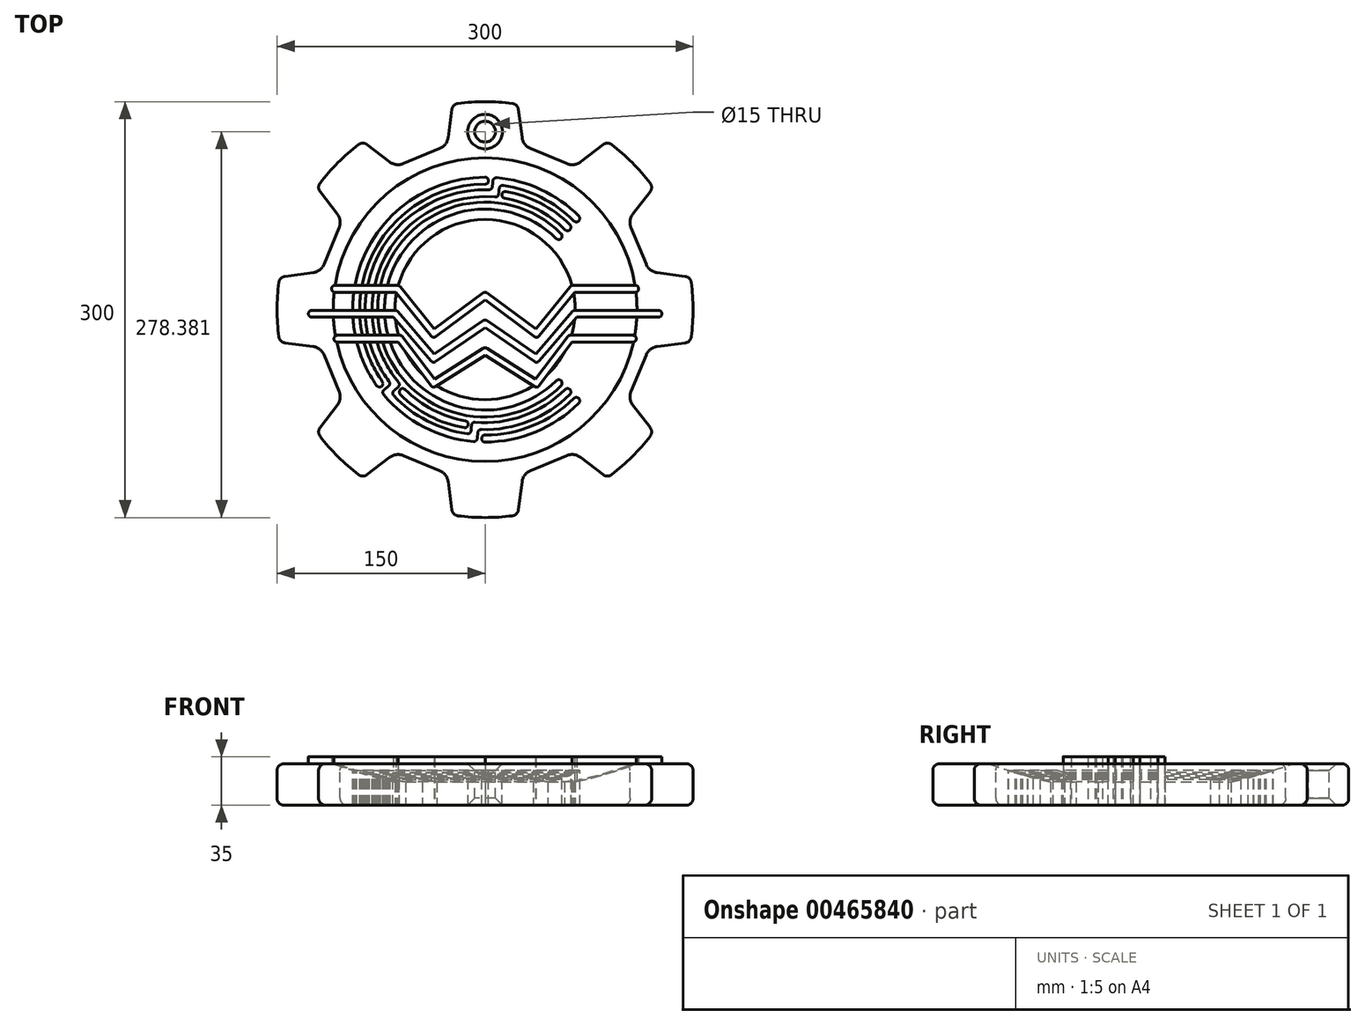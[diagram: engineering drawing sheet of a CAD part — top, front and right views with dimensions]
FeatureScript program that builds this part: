
annotation { "Feature Type Name" : "Feature", "Feature Type Description" : "" }
export const myFeature = defineFeature(function(context is Context, id is Id, definition is map)
    precondition{}
    {
        {
            var Q0;
            Q0=qCreatedBy(makeId("Top.planeOp"),FACE);
            var sketch = newSketch(context, id + "F0", { "sketchPlane" : qUnion([Q0])});
            skPoint(sketch, "E0.center", {"position": v(0, 0) * mm});
            skArc(sketch, "E1", {"start": v(53.03, 53.03) * mm, "mid": v(-75, 0) * mm, "end": v(53.03, -53.03) * mm, "construction": true});
            skLineSegment(sketch, "E2", {"start": v(0, 0) * mm, "end": v(74.3, 74.3) * mm, "construction": true});
            skLineSegment(sketch, "E3", {"start": v(0, 0) * mm, "end": v(73.03, -73.03) * mm, "construction": true});
            skArc(sketch, "E4.0.startCap", {"start": v(54.8, 54.8) * mm, "mid": v(54.8, 51.27) * mm, "end": v(51.27, 51.27) * mm});
            skArc(sketch, "E4.0.endCap", {"start": v(51.27, -51.27) * mm, "mid": v(54.8, -51.27) * mm, "end": v(54.8, -54.8) * mm});
            skArc(sketch, "E4.0.left", {"start": v(51.27, 51.27) * mm, "mid": v(-72.5, 0) * mm, "end": v(51.27, -51.27) * mm});
            skArc(sketch, "E4.0.right", {"start": v(54.8, 54.8) * mm, "mid": v(-77.5, 0) * mm, "end": v(54.8, -54.8) * mm});
            skLineSegment(sketch, "E5", {"start": v(0, 0) * mm, "end": v(18.29, 103.7) * mm, "construction": true});
            skPoint(sketch, "E6", {"position": v(14.59, 82.72) * mm});
            skPoint(sketch, "E7", {"position": v(59.4, 59.4) * mm});
            skArc(sketch, "E8", {"start": v(14.59, 82.72) * mm, "mid": v(10.96, 83.28) * mm, "end": v(7.32, 83.68) * mm, "construction": true});
            skArc(sketch, "E9", {"start": v(59.4, 59.4) * mm, "mid": v(38.79, 74.5) * mm, "end": v(14.59, 82.72) * mm, "construction": true});
            skLineSegment(sketch, "E10", {"start": v(0, 0) * mm, "end": v(9.32, 106.5) * mm, "construction": true});
            skPoint(sketch, "E11", {"position": v(65.76, 65.76) * mm});
            skPoint(sketch, "E12", {"position": v(8.1, 92.65) * mm});
            skPoint(sketch, "E13", {"position": v(7.32, 83.68) * mm});
            skArc(sketch, "E14", {"start": v(8.1, 92.65) * mm, "mid": v(4.06, 92.91) * mm, "end": v(0, 93) * mm, "construction": true});
            skArc(sketch, "E15", {"start": v(65.76, 65.76) * mm, "mid": v(39.3, 84.29) * mm, "end": v(8.1, 92.65) * mm, "construction": true});
            skArc(sketch, "E16.0.startCap", {"start": v(61.16, 61.16) * mm, "mid": v(61.16, 57.63) * mm, "end": v(57.63, 57.63) * mm});
            skArc(sketch, "E16.0.endCap", {"start": v(14.15, 80.26) * mm, "mid": v(12.12, 83.16) * mm, "end": v(15.02, 85.19) * mm});
            skArc(sketch, "E16.0.left", {"start": v(57.63, 57.63) * mm, "mid": v(37.63, 72.3) * mm, "end": v(14.15, 80.26) * mm});
            skArc(sketch, "E16.0.right", {"start": v(61.16, 61.16) * mm, "mid": v(39.94, 76.73) * mm, "end": v(15.02, 85.19) * mm});
            skLineSegment(sketch, "E17", {"start": v(0, 0) * mm, "end": v(-81.14, -68.08) * mm, "construction": true});
            skPoint(sketch, "E18", {"position": v(-64.35, -54) * mm});
            skPoint(sketch, "E19", {"position": v(-71.24, -59.78) * mm});
            skArc(sketch, "E20", {"start": v(-64.35, -54) * mm, "mid": v(-61.93, -56.75) * mm, "end": v(-59.4, -59.4) * mm, "construction": true});
            skArc(sketch, "E21", {"start": v(-71.24, -59.78) * mm, "mid": v(-42.94, -82.5) * mm, "end": v(-8.1, -92.65) * mm, "construction": true});
            skLineSegment(sketch, "E22", {"start": v(0, 0) * mm, "end": v(-9.7, -110.88) * mm, "construction": true});
            skPoint(sketch, "E23", {"position": v(-8.1, -92.65) * mm});
            skPoint(sketch, "E24", {"position": v(-7.32, -83.68) * mm});
            skArc(sketch, "E25", {"start": v(-7.32, -83.68) * mm, "mid": v(28.73, -78.93) * mm, "end": v(59.4, -59.4) * mm, "construction": true});
            skArc(sketch, "E26", {"start": v(-8.1, -92.65) * mm, "mid": v(-4.06, -92.91) * mm, "end": v(0, -93) * mm, "construction": true});
            skLineSegment(sketch, "E27", {"start": v(-64.35, -54) * mm, "end": v(-71.24, -59.78) * mm});
            skLineSegment(sketch, "E28", {"start": v(-7.32, -83.68) * mm, "end": v(-8.1, -92.65) * mm, "construction": true});
            skPoint(sketch, "E29", {"position": v(59.4, -59.4) * mm});
            skArc(sketch, "E30", {"start": v(59.4, -59.4) * mm, "mid": v(84, 0) * mm, "end": v(59.4, 59.4) * mm, "construction": true});
            skLineSegment(sketch, "E31", {"start": v(8.1, 92.65) * mm, "end": v(7.32, 83.68) * mm, "construction": true});
            skArc(sketch, "E32", {"start": v(7.32, 83.68) * mm, "mid": v(-74.5, 38.79) * mm, "end": v(-64.35, -54) * mm, "construction": true});
            skArc(sketch, "E33.0.startCap", {"start": v(5.61, 92.86) * mm, "mid": v(8.32, 95.14) * mm, "end": v(10.6, 92.43) * mm});
            skArc(sketch, "E33.0.endCap", {"start": v(9.81, 83.46) * mm, "mid": v(7.1, 81.19) * mm, "end": v(4.83, 83.9) * mm});
            skLineSegment(sketch, "E33.0.left", {"start": v(10.6, 92.43) * mm, "end": v(9.81, 83.46) * mm});
            skLineSegment(sketch, "E33.0.right", {"start": v(5.61, 92.86) * mm, "end": v(4.83, 83.9) * mm});
            skArc(sketch, "E34.0.startCap", {"start": v(-65.95, -52.08) * mm, "mid": v(-62.43, -52.39) * mm, "end": v(-62.74, -55.9) * mm});
            skArc(sketch, "E34.0.endCap", {"start": v(-69.64, -61.7) * mm, "mid": v(-73.16, -61.39) * mm, "end": v(-72.85, -57.86) * mm});
            skLineSegment(sketch, "E34.0.left", {"start": v(-62.74, -55.9) * mm, "end": v(-69.64, -61.7) * mm});
            skLineSegment(sketch, "E34.0.right", {"start": v(-65.95, -52.08) * mm, "end": v(-72.85, -57.86) * mm});
            skArc(sketch, "E34.1.startCap", {"start": v(-9.81, -83.46) * mm, "mid": v(-7.1, -81.19) * mm, "end": v(-4.83, -83.9) * mm});
            skArc(sketch, "E34.1.endCap", {"start": v(-5.61, -92.86) * mm, "mid": v(-8.32, -95.14) * mm, "end": v(-10.6, -92.43) * mm});
            skLineSegment(sketch, "E34.1.left", {"start": v(-4.83, -83.9) * mm, "end": v(-5.61, -92.86) * mm});
            skLineSegment(sketch, "E34.1.right", {"start": v(-9.81, -83.46) * mm, "end": v(-10.6, -92.43) * mm});
            skArc(sketch, "E35.0.startCap", {"start": v(-73.16, -61.39) * mm, "mid": v(-72.85, -57.86) * mm, "end": v(-69.33, -58.17) * mm});
            skArc(sketch, "E35.0.endCap", {"start": v(-7.89, -90.16) * mm, "mid": v(-5.61, -92.86) * mm, "end": v(-8.32, -95.14) * mm});
            skArc(sketch, "E35.0.left", {"start": v(-69.33, -58.17) * mm, "mid": v(-41.79, -80.27) * mm, "end": v(-7.89, -90.16) * mm});
            skArc(sketch, "E35.0.right", {"start": v(-73.16, -61.39) * mm, "mid": v(-44.1, -84.7) * mm, "end": v(-8.32, -95.14) * mm});
            skArc(sketch, "E35.1.startCap", {"start": v(-7.54, -86.17) * mm, "mid": v(-9.81, -83.46) * mm, "end": v(-7.1, -81.19) * mm});
            skArc(sketch, "E35.1.endCap", {"start": v(57.63, -57.63) * mm, "mid": v(61.16, -57.63) * mm, "end": v(61.16, -61.16) * mm});
            skArc(sketch, "E35.1.left", {"start": v(-7.1, -81.19) * mm, "mid": v(27.87, -76.58) * mm, "end": v(57.63, -57.63) * mm});
            skArc(sketch, "E35.1.right", {"start": v(-7.54, -86.17) * mm, "mid": v(29.58, -81.28) * mm, "end": v(61.16, -61.16) * mm});
            skArc(sketch, "E35.2.startCap", {"start": v(7.54, 86.17) * mm, "mid": v(9.81, 83.46) * mm, "end": v(7.1, 81.19) * mm});
            skArc(sketch, "E35.2.endCap", {"start": v(-62.43, -52.39) * mm, "mid": v(-62.74, -55.9) * mm, "end": v(-66.26, -55.6) * mm});
            skArc(sketch, "E35.2.left", {"start": v(7.1, 81.19) * mm, "mid": v(-72.3, 37.63) * mm, "end": v(-62.43, -52.39) * mm});
            skArc(sketch, "E35.2.right", {"start": v(7.54, 86.17) * mm, "mid": v(-76.73, 39.94) * mm, "end": v(-66.26, -55.6) * mm});
            skArc(sketch, "E35.3.startCap", {"start": v(67.53, 67.53) * mm, "mid": v(67.53, 64) * mm, "end": v(64, 64) * mm});
            skArc(sketch, "E35.3.endCap", {"start": v(7.89, 90.16) * mm, "mid": v(5.61, 92.86) * mm, "end": v(8.32, 95.14) * mm});
            skArc(sketch, "E35.3.left", {"start": v(64, 64) * mm, "mid": v(38.25, 82.02) * mm, "end": v(7.89, 90.16) * mm});
            skArc(sketch, "E35.3.right", {"start": v(67.53, 67.53) * mm, "mid": v(40.36, 86.55) * mm, "end": v(8.32, 95.14) * mm});
            skLineSegment(sketch, "E36", {"start": v(0, 0) * mm, "end": v(-93.02, -65.13) * mm, "construction": true});
            skPoint(sketch, "E37", {"position": v(-76.18, -53.34) * mm});
            skArc(sketch, "E38", {"start": v(-76.18, -53.34) * mm, "mid": v(-73.78, -56.61) * mm, "end": v(-71.24, -59.78) * mm, "construction": true});
            skLineSegment(sketch, "E39", {"start": v(0, 0) * mm, "end": v(0, -111.62) * mm, "construction": true});
            skPoint(sketch, "E40", {"position": v(0, -93) * mm});
            skArc(sketch, "E41", {"start": v(0, -93) * mm, "mid": v(35.59, -85.92) * mm, "end": v(65.76, -65.76) * mm, "construction": true});
            skPoint(sketch, "E42", {"position": v(65.76, -65.76) * mm});
            skArc(sketch, "E43", {"start": v(65.76, -65.76) * mm, "mid": v(93, 0) * mm, "end": v(65.76, 65.76) * mm, "construction": true});
            skLineSegment(sketch, "E44", {"start": v(0, 0) * mm, "end": v(0, 108.9) * mm, "construction": true});
            skPoint(sketch, "E45", {"position": v(0, 93) * mm});
            skArc(sketch, "E46", {"start": v(0, 93) * mm, "mid": v(-82.5, 42.94) * mm, "end": v(-76.18, -53.34) * mm, "construction": true});
            skArc(sketch, "E47.0.startCap", {"start": v(0, 95.5) * mm, "mid": v(2.5, 93) * mm, "end": v(0, 90.5) * mm});
            skArc(sketch, "E47.0.endCap", {"start": v(-74.13, -51.9) * mm, "mid": v(-74.75, -55.4) * mm, "end": v(-78.23, -54.78) * mm});
            skArc(sketch, "E47.0.left", {"start": v(0, 90.5) * mm, "mid": v(-80.27, 41.79) * mm, "end": v(-74.13, -51.9) * mm});
            skArc(sketch, "E47.0.right", {"start": v(0, 95.5) * mm, "mid": v(-84.7, 44.1) * mm, "end": v(-78.23, -54.78) * mm});
            skArc(sketch, "E47.1.startCap", {"start": v(0, -95.5) * mm, "mid": v(-2.5, -93) * mm, "end": v(0, -90.5) * mm});
            skArc(sketch, "E47.1.endCap", {"start": v(64, -64) * mm, "mid": v(67.53, -64) * mm, "end": v(67.53, -67.53) * mm});
            skArc(sketch, "E47.1.left", {"start": v(0, -90.5) * mm, "mid": v(34.63, -83.61) * mm, "end": v(64, -64) * mm});
            skArc(sketch, "E47.1.right", {"start": v(0, -95.5) * mm, "mid": v(36.55, -88.23) * mm, "end": v(67.53, -67.53) * mm});
            skLineSegment(sketch, "E48", {"start": v(0, 0) * mm, "end": v(-91.1, -91.1) * mm, "construction": true});
            skLineSegment(sketch, "E49", {"start": v(0, 0) * mm, "end": v(-19.76, -112.08) * mm, "construction": true});
            skPoint(sketch, "E50", {"position": v(-59.4, -59.4) * mm});
            skPoint(sketch, "E51", {"position": v(-14.59, -82.72) * mm});
            skArc(sketch, "E52", {"start": v(-59.4, -59.4) * mm, "mid": v(-38.79, -74.5) * mm, "end": v(-14.59, -82.72) * mm, "construction": true});
            skArc(sketch, "E53", {"start": v(-14.59, -82.72) * mm, "mid": v(-10.96, -83.28) * mm, "end": v(-7.32, -83.68) * mm, "construction": true});
            skArc(sketch, "E54.0.startCap", {"start": v(-61.16, -61.16) * mm, "mid": v(-61.16, -57.63) * mm, "end": v(-57.63, -57.63) * mm});
            skArc(sketch, "E54.0.endCap", {"start": v(-14.15, -80.26) * mm, "mid": v(-12.12, -83.16) * mm, "end": v(-15.02, -85.19) * mm});
            skArc(sketch, "E54.0.left", {"start": v(-57.63, -57.63) * mm, "mid": v(-37.63, -72.3) * mm, "end": v(-14.15, -80.26) * mm});
            skArc(sketch, "E54.0.right", {"start": v(-61.16, -61.16) * mm, "mid": v(-39.94, -76.73) * mm, "end": v(-15.02, -85.19) * mm});
            skSolve(sketch);
        }
        {
            var Q0;
            Q0=qCreatedBy(makeId("Top.planeOp"),FACE);
            var sketch = newSketch(context, id + "F1", { "sketchPlane" : qUnion([Q0])});
            skCircle(sketch, "E55", {"center": v(0, 0) * mm, "radius": 150 * mm});
            skLineSegment(sketch, "E56", {"start": v(-35, 145.86) * mm, "end": v(-20, 119.88) * mm});
            skLineSegment(sketch, "E57", {"start": v(-20, 119.88) * mm, "end": v(20, 119.88) * mm});
            skLineSegment(sketch, "E58", {"start": v(20, 119.88) * mm, "end": v(35, 145.86) * mm});
            skLineSegment(sketch, "E59.1.0", {"start": v(-127.89, 78.39) * mm, "end": v(-98.9, 70.62) * mm});
            skLineSegment(sketch, "E59.1.1", {"start": v(-98.9, 70.62) * mm, "end": v(-70.62, 98.9) * mm});
            skLineSegment(sketch, "E59.1.2", {"start": v(-70.62, 98.9) * mm, "end": v(-78.39, 127.89) * mm});
            skLineSegment(sketch, "E59.2.0", {"start": v(-145.86, -35) * mm, "end": v(-119.88, -20) * mm});
            skLineSegment(sketch, "E59.2.1", {"start": v(-119.88, -20) * mm, "end": v(-119.88, 20) * mm});
            skLineSegment(sketch, "E59.2.2", {"start": v(-119.88, 20) * mm, "end": v(-145.86, 35) * mm});
            skLineSegment(sketch, "E59.3.0", {"start": v(-78.39, -127.89) * mm, "end": v(-70.62, -98.9) * mm});
            skLineSegment(sketch, "E59.3.1", {"start": v(-70.62, -98.9) * mm, "end": v(-98.9, -70.62) * mm});
            skLineSegment(sketch, "E59.3.2", {"start": v(-98.9, -70.62) * mm, "end": v(-127.89, -78.39) * mm});
            skLineSegment(sketch, "E59.4.0", {"start": v(35, -145.86) * mm, "end": v(20, -119.88) * mm});
            skLineSegment(sketch, "E59.4.1", {"start": v(20, -119.88) * mm, "end": v(-20, -119.88) * mm});
            skLineSegment(sketch, "E59.4.2", {"start": v(-20, -119.88) * mm, "end": v(-35, -145.86) * mm});
            skLineSegment(sketch, "E59.5.0", {"start": v(127.89, -78.39) * mm, "end": v(98.9, -70.62) * mm});
            skLineSegment(sketch, "E59.5.1", {"start": v(98.9, -70.62) * mm, "end": v(70.62, -98.9) * mm});
            skLineSegment(sketch, "E59.5.2", {"start": v(70.62, -98.9) * mm, "end": v(78.39, -127.89) * mm});
            skLineSegment(sketch, "E59.6.0", {"start": v(145.86, 35) * mm, "end": v(119.88, 20) * mm});
            skLineSegment(sketch, "E59.6.1", {"start": v(119.88, 20) * mm, "end": v(119.88, -20) * mm});
            skLineSegment(sketch, "E59.6.2", {"start": v(119.88, -20) * mm, "end": v(145.86, -35) * mm});
            skLineSegment(sketch, "E59.7.0", {"start": v(78.39, 127.89) * mm, "end": v(70.62, 98.9) * mm});
            skLineSegment(sketch, "E59.7.1", {"start": v(70.62, 98.9) * mm, "end": v(98.9, 70.62) * mm});
            skLineSegment(sketch, "E59.7.2", {"start": v(98.9, 70.62) * mm, "end": v(127.89, 78.39) * mm});
            skCircle(sketch, "E60", {"center": v(0, 0) * mm, "radius": 65 * mm});
            skSolve(sketch);
        }
        {
            var Q0;
            Q0=qCreatedBy(makeId("Top.planeOp"),FACE);
            var sketch = newSketch(context, id + "F2", { "sketchPlane" : qUnion([Q0])});
            skLineSegment(sketch, "E61", {"start": v(-108.25, 15) * mm, "end": v(-63.25, 15) * mm, "construction": true});
            skLineSegment(sketch, "E62", {"start": v(-63.25, 15) * mm, "end": v(-37, -17.44) * mm, "construction": true});
            skLineSegment(sketch, "E63", {"start": v(-37, -17.44) * mm, "end": v(0, 10) * mm, "construction": true});
            skLineSegment(sketch, "E64", {"start": v(0, 10) * mm, "end": v(37, -17.44) * mm, "construction": true});
            skLineSegment(sketch, "E65", {"start": v(37, -17.44) * mm, "end": v(63.25, 15) * mm, "construction": true});
            skLineSegment(sketch, "E66", {"start": v(63.25, 15) * mm, "end": v(108.25, 15) * mm, "construction": true});
            skLineSegment(sketch, "E67", {"start": v(-124.93, -3) * mm, "end": v(-64.93, -3) * mm, "construction": true});
            skLineSegment(sketch, "E68", {"start": v(-64.93, -3) * mm, "end": v(-37, -35.44) * mm, "construction": true});
            skLineSegment(sketch, "E69", {"start": v(-37, -35.44) * mm, "end": v(0, -10) * mm, "construction": true});
            skLineSegment(sketch, "E70", {"start": v(0, -10) * mm, "end": v(37, -35.44) * mm, "construction": true});
            skLineSegment(sketch, "E71", {"start": v(37, -35.44) * mm, "end": v(64.93, -3) * mm, "construction": true});
            skLineSegment(sketch, "E72", {"start": v(64.93, -3) * mm, "end": v(124.93, -3) * mm, "construction": true});
            skLineSegment(sketch, "E73", {"start": v(-106.51, -21) * mm, "end": v(-61.51, -21) * mm, "construction": true});
            skLineSegment(sketch, "E74", {"start": v(-61.51, -21) * mm, "end": v(-37, -53.44) * mm, "construction": true});
            skLineSegment(sketch, "E75", {"start": v(-37, -53.44) * mm, "end": v(0, -30) * mm, "construction": true});
            skLineSegment(sketch, "E76", {"start": v(0, -30) * mm, "end": v(37, -53.44) * mm, "construction": true});
            skLineSegment(sketch, "E77", {"start": v(37, -53.44) * mm, "end": v(61.51, -21) * mm, "construction": true});
            skLineSegment(sketch, "E78", {"start": v(61.51, -21) * mm, "end": v(106.51, -21) * mm, "construction": true});
            skLineSegment(sketch, "E79", {"start": v(0, 45.3) * mm, "end": v(0, -49.42) * mm, "construction": true});
            skCircle(sketch, "E80", {"center": v(0, 0) * mm, "radius": 65 * mm, "construction": true});
            skLineSegment(sketch, "E81", {"start": v(-37, -53.44) * mm, "end": v(-37, 14.46) * mm, "construction": true});
            skArc(sketch, "E82.0.startCap", {"start": v(-106.51, -23.5) * mm, "mid": v(-109.01, -21) * mm, "end": v(-106.51, -18.5) * mm});
            skArc(sketch, "E82.0.endCap", {"start": v(-61.51, -18.5) * mm, "mid": v(-59.01, -21) * mm, "end": v(-61.51, -23.5) * mm});
            skLineSegment(sketch, "E82.0.left", {"start": v(-106.51, -18.5) * mm, "end": v(-61.51, -18.5) * mm});
            skLineSegment(sketch, "E82.0.right", {"start": v(-106.51, -23.5) * mm, "end": v(-61.51, -23.5) * mm});
            skArc(sketch, "E82.1.startCap", {"start": v(-124.93, -5.5) * mm, "mid": v(-127.43, -3) * mm, "end": v(-124.93, -0.5) * mm});
            skArc(sketch, "E82.1.endCap", {"start": v(-64.93, -0.5) * mm, "mid": v(-62.43, -3) * mm, "end": v(-64.93, -5.5) * mm});
            skLineSegment(sketch, "E82.1.left", {"start": v(-124.93, -0.5) * mm, "end": v(-64.93, -0.5) * mm});
            skLineSegment(sketch, "E82.1.right", {"start": v(-124.93, -5.5) * mm, "end": v(-64.93, -5.5) * mm});
            skArc(sketch, "E82.2.startCap", {"start": v(-108.25, 12.5) * mm, "mid": v(-110.75, 15) * mm, "end": v(-108.25, 17.5) * mm});
            skArc(sketch, "E82.2.endCap", {"start": v(-63.25, 17.5) * mm, "mid": v(-60.75, 15) * mm, "end": v(-63.25, 12.5) * mm});
            skLineSegment(sketch, "E82.2.left", {"start": v(-108.25, 17.5) * mm, "end": v(-63.25, 17.5) * mm});
            skLineSegment(sketch, "E82.2.right", {"start": v(-108.25, 12.5) * mm, "end": v(-63.25, 12.5) * mm});
            skArc(sketch, "E82.3.startCap", {"start": v(-65.19, 13.43) * mm, "mid": v(-64.82, 16.94) * mm, "end": v(-61.3, 16.57) * mm});
            skArc(sketch, "E82.3.endCap", {"start": v(-35.06, -15.87) * mm, "mid": v(-35.43, -19.39) * mm, "end": v(-38.94, -19.01) * mm});
            skLineSegment(sketch, "E82.3.left", {"start": v(-61.3, 16.57) * mm, "end": v(-35.06, -15.87) * mm});
            skLineSegment(sketch, "E82.3.right", {"start": v(-65.19, 13.43) * mm, "end": v(-38.94, -19.01) * mm});
            skArc(sketch, "E82.4.startCap", {"start": v(-66.83, -4.63) * mm, "mid": v(-66.56, -1.1) * mm, "end": v(-63.04, -1.37) * mm});
            skArc(sketch, "E82.4.endCap", {"start": v(-35.1, -33.81) * mm, "mid": v(-35.37, -37.34) * mm, "end": v(-38.9, -37.07) * mm});
            skLineSegment(sketch, "E82.4.left", {"start": v(-63.04, -1.37) * mm, "end": v(-35.1, -33.81) * mm});
            skLineSegment(sketch, "E82.4.right", {"start": v(-66.83, -4.63) * mm, "end": v(-38.9, -37.07) * mm});
            skArc(sketch, "E82.5.startCap", {"start": v(-63.5, -22.5) * mm, "mid": v(-63.02, -19) * mm, "end": v(-59.52, -19.5) * mm});
            skArc(sketch, "E82.5.endCap", {"start": v(-35, -51.93) * mm, "mid": v(-35.5, -55.44) * mm, "end": v(-39, -54.95) * mm});
            skLineSegment(sketch, "E82.5.left", {"start": v(-59.52, -19.5) * mm, "end": v(-35, -51.93) * mm});
            skLineSegment(sketch, "E82.5.right", {"start": v(-63.5, -22.5) * mm, "end": v(-39, -54.95) * mm});
            skArc(sketch, "E82.6.startCap", {"start": v(-35.51, -19.45) * mm, "mid": v(-39, -18.93) * mm, "end": v(-38.49, -15.43) * mm});
            skArc(sketch, "E82.6.endCap", {"start": v(-1.49, 12) * mm, "mid": v(2, 11.49) * mm, "end": v(1.49, 8) * mm});
            skLineSegment(sketch, "E82.6.left", {"start": v(-38.49, -15.43) * mm, "end": v(-1.49, 12) * mm});
            skLineSegment(sketch, "E82.6.right", {"start": v(-35.51, -19.45) * mm, "end": v(1.49, 8) * mm});
            skArc(sketch, "E82.7.startCap", {"start": v(-35.58, -37.5) * mm, "mid": v(-39.06, -36.86) * mm, "end": v(-38.42, -33.38) * mm});
            skArc(sketch, "E82.7.endCap", {"start": v(-1.42, -7.94) * mm, "mid": v(2.06, -8.58) * mm, "end": v(1.42, -12.06) * mm});
            skLineSegment(sketch, "E82.7.left", {"start": v(-38.42, -33.38) * mm, "end": v(-1.42, -7.94) * mm});
            skLineSegment(sketch, "E82.7.right", {"start": v(-35.58, -37.5) * mm, "end": v(1.42, -12.06) * mm});
            skArc(sketch, "E82.8.startCap", {"start": v(-35.66, -55.55) * mm, "mid": v(-39.11, -54.78) * mm, "end": v(-38.34, -51.33) * mm});
            skArc(sketch, "E82.8.endCap", {"start": v(-1.34, -27.89) * mm, "mid": v(2.11, -28.66) * mm, "end": v(1.34, -32.11) * mm});
            skLineSegment(sketch, "E82.8.left", {"start": v(-38.34, -51.33) * mm, "end": v(-1.34, -27.89) * mm});
            skLineSegment(sketch, "E82.8.right", {"start": v(-35.66, -55.55) * mm, "end": v(1.34, -32.11) * mm});
            skArc(sketch, "E82.9.startCap", {"start": v(-1.34, -32.11) * mm, "mid": v(-2.11, -28.66) * mm, "end": v(1.34, -27.89) * mm});
            skArc(sketch, "E82.9.endCap", {"start": v(38.34, -51.33) * mm, "mid": v(39.11, -54.78) * mm, "end": v(35.66, -55.55) * mm});
            skLineSegment(sketch, "E82.9.left", {"start": v(1.34, -27.89) * mm, "end": v(38.34, -51.33) * mm});
            skLineSegment(sketch, "E82.9.right", {"start": v(-1.34, -32.11) * mm, "end": v(35.66, -55.55) * mm});
            skArc(sketch, "E82.10.startCap", {"start": v(-1.42, -12.06) * mm, "mid": v(-2.06, -8.58) * mm, "end": v(1.42, -7.94) * mm});
            skArc(sketch, "E82.10.endCap", {"start": v(38.42, -33.38) * mm, "mid": v(39.06, -36.86) * mm, "end": v(35.58, -37.5) * mm});
            skLineSegment(sketch, "E82.10.left", {"start": v(1.42, -7.94) * mm, "end": v(38.42, -33.38) * mm});
            skLineSegment(sketch, "E82.10.right", {"start": v(-1.42, -12.06) * mm, "end": v(35.58, -37.5) * mm});
            skArc(sketch, "E82.11.startCap", {"start": v(-1.49, 8) * mm, "mid": v(-2, 11.49) * mm, "end": v(1.49, 12) * mm});
            skArc(sketch, "E82.11.endCap", {"start": v(38.49, -15.43) * mm, "mid": v(39, -18.93) * mm, "end": v(35.51, -19.45) * mm});
            skLineSegment(sketch, "E82.11.left", {"start": v(1.49, 12) * mm, "end": v(38.49, -15.43) * mm});
            skLineSegment(sketch, "E82.11.right", {"start": v(-1.49, 8) * mm, "end": v(35.51, -19.45) * mm});
            skArc(sketch, "E82.12.startCap", {"start": v(38.94, -19.01) * mm, "mid": v(35.43, -19.39) * mm, "end": v(35.06, -15.87) * mm});
            skArc(sketch, "E82.12.endCap", {"start": v(61.3, 16.57) * mm, "mid": v(64.82, 16.94) * mm, "end": v(65.19, 13.43) * mm});
            skLineSegment(sketch, "E82.12.left", {"start": v(35.06, -15.87) * mm, "end": v(61.3, 16.57) * mm});
            skLineSegment(sketch, "E82.12.right", {"start": v(38.94, -19.01) * mm, "end": v(65.19, 13.43) * mm});
            skArc(sketch, "E82.13.startCap", {"start": v(38.9, -37.07) * mm, "mid": v(35.37, -37.34) * mm, "end": v(35.1, -33.81) * mm});
            skArc(sketch, "E82.13.endCap", {"start": v(63.04, -1.37) * mm, "mid": v(66.56, -1.1) * mm, "end": v(66.83, -4.63) * mm});
            skLineSegment(sketch, "E82.13.left", {"start": v(35.1, -33.81) * mm, "end": v(63.04, -1.37) * mm});
            skLineSegment(sketch, "E82.13.right", {"start": v(38.9, -37.07) * mm, "end": v(66.83, -4.63) * mm});
            skArc(sketch, "E82.14.startCap", {"start": v(39, -54.95) * mm, "mid": v(35.5, -55.44) * mm, "end": v(35, -51.93) * mm});
            skArc(sketch, "E82.14.endCap", {"start": v(59.52, -19.5) * mm, "mid": v(63.02, -19) * mm, "end": v(63.5, -22.5) * mm});
            skLineSegment(sketch, "E82.14.left", {"start": v(35, -51.93) * mm, "end": v(59.52, -19.5) * mm});
            skLineSegment(sketch, "E82.14.right", {"start": v(39, -54.95) * mm, "end": v(63.5, -22.5) * mm});
            skArc(sketch, "E82.15.startCap", {"start": v(61.51, -23.5) * mm, "mid": v(59.01, -21) * mm, "end": v(61.51, -18.5) * mm});
            skArc(sketch, "E82.15.endCap", {"start": v(106.51, -18.5) * mm, "mid": v(109.01, -21) * mm, "end": v(106.51, -23.5) * mm});
            skLineSegment(sketch, "E82.15.left", {"start": v(61.51, -18.5) * mm, "end": v(106.51, -18.5) * mm});
            skLineSegment(sketch, "E82.15.right", {"start": v(61.51, -23.5) * mm, "end": v(106.51, -23.5) * mm});
            skArc(sketch, "E82.16.startCap", {"start": v(64.93, -5.5) * mm, "mid": v(62.43, -3) * mm, "end": v(64.93, -0.5) * mm});
            skArc(sketch, "E82.16.endCap", {"start": v(124.93, -0.5) * mm, "mid": v(127.43, -3) * mm, "end": v(124.93, -5.5) * mm});
            skLineSegment(sketch, "E82.16.left", {"start": v(64.93, -0.5) * mm, "end": v(124.93, -0.5) * mm});
            skLineSegment(sketch, "E82.16.right", {"start": v(64.93, -5.5) * mm, "end": v(124.93, -5.5) * mm});
            skArc(sketch, "E82.17.startCap", {"start": v(63.25, 12.5) * mm, "mid": v(60.75, 15) * mm, "end": v(63.25, 17.5) * mm});
            skArc(sketch, "E82.17.endCap", {"start": v(108.25, 17.5) * mm, "mid": v(110.75, 15) * mm, "end": v(108.25, 12.5) * mm});
            skLineSegment(sketch, "E82.17.left", {"start": v(63.25, 17.5) * mm, "end": v(108.25, 17.5) * mm});
            skLineSegment(sketch, "E82.17.right", {"start": v(63.25, 12.5) * mm, "end": v(108.25, 12.5) * mm});
            skSolve(sketch);
        }
        {
            var Q0;
            {var subQ8=sQuery(id+"F1.wireOp",EDGE,"E56");Q0=makeQuery(id+"F1.imprint","IMPRINT",FACE,{"disambiguationData":[TD([[makeQuery(id+"F1.imprint","IMPRINT",EDGE,{"derivedFrom":subQ8}),-1.0]])]});}
            extrude(context, id + "F3", {"entities" : qUnion([Q0]), "endBound" : BoundingType.SYMMETRIC, "depth" : 30 * mm});
        }
        {
            var Q0;
            Q0=makeQuery(id+"F3.opExtrude","SWEPT_BODY",BODY,{"disambiguationData":[OSD([sQuery(id+"F1.wireOp",EDGE,"E55"),sQuery(id+"F1.wireOp",EDGE,"E56"),sQuery(id+"F1.wireOp",EDGE,"E57"),sQuery(id+"F1.wireOp",EDGE,"E58"),sQuery(id+"F1.wireOp",EDGE,"E59.1.0"),sQuery(id+"F1.wireOp",EDGE,"E59.1.1"),sQuery(id+"F1.wireOp",EDGE,"E59.1.2"),sQuery(id+"F1.wireOp",EDGE,"E59.2.0"),sQuery(id+"F1.wireOp",EDGE,"E59.2.1"),sQuery(id+"F1.wireOp",EDGE,"E59.2.2"),sQuery(id+"F1.wireOp",EDGE,"E59.3.0"),sQuery(id+"F1.wireOp",EDGE,"E59.3.1"),sQuery(id+"F1.wireOp",EDGE,"E59.3.2"),sQuery(id+"F1.wireOp",EDGE,"E59.4.0"),sQuery(id+"F1.wireOp",EDGE,"E59.4.1"),sQuery(id+"F1.wireOp",EDGE,"E59.4.2"),sQuery(id+"F1.wireOp",EDGE,"E59.5.0"),sQuery(id+"F1.wireOp",EDGE,"E59.5.1"),sQuery(id+"F1.wireOp",EDGE,"E59.5.2"),sQuery(id+"F1.wireOp",EDGE,"E59.6.0"),sQuery(id+"F1.wireOp",EDGE,"E59.6.1"),sQuery(id+"F1.wireOp",EDGE,"E59.6.2"),sQuery(id+"F1.wireOp",EDGE,"E59.7.0"),sQuery(id+"F1.wireOp",EDGE,"E59.7.1"),sQuery(id+"F1.wireOp",EDGE,"E59.7.2"),sQuery(id+"F1.wireOp",EDGE,"E60")])]});
            var Q1;
            Q1=makeQuery(id+"F3.opExtrude","CAP_EDGE",EDGE,{"disambiguationData":[OSD([sQuery(id+"F1.wireOp",EDGE,"E60")])],"isStart":true});
            transform(context, id + "F4", {"entities" : qUnion([Q0]), "transformType" : TransformType.ROTATION, "transformAxis" : qUnion([Q1]), "angle" : 22.5 * degree, "makeCopy" : false});
        }
        {
            var Q0;
            Q0=qSketchRegion(id+"F0",true);
            extrude(context, id + "F5", {"entities" : qUnion([Q0]), "operationType" : NewBodyOperationType.REMOVE, "endBound" : BoundingType.SYMMETRIC, "oppositeDirection" : true, "depth" : 74 * mm});
        }
        {
            var Q0;
            Q0=makeQuery(id+"F5.boolean.opBoolean","COPY",EDGE,{"derivedFrom":makeQuery(id+"F5.opExtrude","SWEPT_EDGE",EDGE,{"disambiguationData":[OSD([sQuery(id+"F0.wireOp",EDGE,"E34.0.right"),sQuery(id+"F0.wireOp",EDGE,"E35.2.right")])]})});
            var Q1;
            Q1=makeQuery(id+"F5.boolean.opBoolean","COPY",EDGE,{"derivedFrom":makeQuery(id+"F5.opExtrude","SWEPT_EDGE",EDGE,{"disambiguationData":[OSD([sQuery(id+"F0.wireOp",EDGE,"E34.1.right"),sQuery(id+"F0.wireOp",EDGE,"E35.0.left")])]})});
            var Q2;
            Q2=makeQuery(id+"F5.boolean.opBoolean","COPY",EDGE,{"derivedFrom":makeQuery(id+"F5.opExtrude","SWEPT_EDGE",EDGE,{"disambiguationData":[OSD([sQuery(id+"F0.wireOp",EDGE,"E34.1.left"),sQuery(id+"F0.wireOp",EDGE,"E35.1.right")])]})});
            var Q3;
            Q3=makeQuery(id+"F5.boolean.opBoolean","COPY",EDGE,{"derivedFrom":makeQuery(id+"F5.opExtrude","SWEPT_EDGE",EDGE,{"disambiguationData":[OSD([sQuery(id+"F0.wireOp",EDGE,"E34.0.left"),sQuery(id+"F0.wireOp",EDGE,"E35.0.left")])]})});
            var Q4;
            Q4=makeQuery(id+"F5.boolean.opBoolean","COPY",EDGE,{"derivedFrom":makeQuery(id+"F5.opExtrude","SWEPT_EDGE",EDGE,{"disambiguationData":[OSD([sQuery(id+"F0.wireOp",EDGE,"E33.0.left"),sQuery(id+"F0.wireOp",EDGE,"E35.3.left")])]})});
            var Q5;
            Q5=makeQuery(id+"F5.boolean.opBoolean","COPY",EDGE,{"derivedFrom":makeQuery(id+"F5.opExtrude","SWEPT_EDGE",EDGE,{"disambiguationData":[OSD([sQuery(id+"F0.wireOp",EDGE,"E33.0.right"),sQuery(id+"F0.wireOp",EDGE,"E35.2.right")])]})});
            fillet(context, id + "F6", {"entities" : qUnion([Q0, Q1, Q2, Q3, Q4, Q5]), "radius" : 2.5 * mm, "tangentPropagation" : true, "allowEdgeOverflow" : false});
        }
        {
            var Q0;
            Q0=makeQuery(id+"F3.opExtrude","SWEPT_EDGE",EDGE,{"disambiguationData":[OSD([sQuery(id+"F1.wireOp",EDGE,"E59.1.0"),sQuery(id+"F1.wireOp",EDGE,"E59.1.1")])]});
            var Q1;
            Q1=makeQuery(id+"F3.opExtrude","SWEPT_EDGE",EDGE,{"disambiguationData":[OSD([sQuery(id+"F1.wireOp",EDGE,"E59.1.1"),sQuery(id+"F1.wireOp",EDGE,"E59.1.2")])]});
            var Q2;
            Q2=makeQuery(id+"F3.opExtrude","SWEPT_EDGE",EDGE,{"disambiguationData":[OSD([sQuery(id+"F1.wireOp",EDGE,"E56"),sQuery(id+"F1.wireOp",EDGE,"E57")])]});
            var Q3;
            Q3=makeQuery(id+"F3.opExtrude","SWEPT_EDGE",EDGE,{"disambiguationData":[OSD([sQuery(id+"F1.wireOp",EDGE,"E57"),sQuery(id+"F1.wireOp",EDGE,"E58")])]});
            var Q4;
            Q4=makeQuery(id+"F3.opExtrude","SWEPT_EDGE",EDGE,{"disambiguationData":[OSD([sQuery(id+"F1.wireOp",EDGE,"E59.7.0"),sQuery(id+"F1.wireOp",EDGE,"E59.7.1")])]});
            var Q5;
            Q5=makeQuery(id+"F3.opExtrude","SWEPT_EDGE",EDGE,{"disambiguationData":[OSD([sQuery(id+"F1.wireOp",EDGE,"E59.7.1"),sQuery(id+"F1.wireOp",EDGE,"E59.7.2")])]});
            var Q6;
            Q6=makeQuery(id+"F3.opExtrude","SWEPT_EDGE",EDGE,{"disambiguationData":[OSD([sQuery(id+"F1.wireOp",EDGE,"E59.6.0"),sQuery(id+"F1.wireOp",EDGE,"E59.6.1")])]});
            var Q7;
            Q7=makeQuery(id+"F3.opExtrude","SWEPT_EDGE",EDGE,{"disambiguationData":[OSD([sQuery(id+"F1.wireOp",EDGE,"E59.6.1"),sQuery(id+"F1.wireOp",EDGE,"E59.6.2")])]});
            var Q8;
            Q8=makeQuery(id+"F3.opExtrude","SWEPT_EDGE",EDGE,{"disambiguationData":[OSD([sQuery(id+"F1.wireOp",EDGE,"E59.5.0"),sQuery(id+"F1.wireOp",EDGE,"E59.5.1")])]});
            var Q9;
            Q9=makeQuery(id+"F3.opExtrude","SWEPT_EDGE",EDGE,{"disambiguationData":[OSD([sQuery(id+"F1.wireOp",EDGE,"E59.5.1"),sQuery(id+"F1.wireOp",EDGE,"E59.5.2")])]});
            var Q10;
            Q10=makeQuery(id+"F3.opExtrude","SWEPT_EDGE",EDGE,{"disambiguationData":[OSD([sQuery(id+"F1.wireOp",EDGE,"E59.4.0"),sQuery(id+"F1.wireOp",EDGE,"E59.4.1")])]});
            var Q11;
            Q11=makeQuery(id+"F3.opExtrude","SWEPT_EDGE",EDGE,{"disambiguationData":[OSD([sQuery(id+"F1.wireOp",EDGE,"E59.4.1"),sQuery(id+"F1.wireOp",EDGE,"E59.4.2")])]});
            var Q12;
            Q12=makeQuery(id+"F3.opExtrude","SWEPT_EDGE",EDGE,{"disambiguationData":[OSD([sQuery(id+"F1.wireOp",EDGE,"E59.3.0"),sQuery(id+"F1.wireOp",EDGE,"E59.3.1")])]});
            var Q13;
            Q13=makeQuery(id+"F3.opExtrude","SWEPT_EDGE",EDGE,{"disambiguationData":[OSD([sQuery(id+"F1.wireOp",EDGE,"E59.3.1"),sQuery(id+"F1.wireOp",EDGE,"E59.3.2")])]});
            var Q14;
            Q14=makeQuery(id+"F3.opExtrude","SWEPT_EDGE",EDGE,{"disambiguationData":[OSD([sQuery(id+"F1.wireOp",EDGE,"E59.2.0"),sQuery(id+"F1.wireOp",EDGE,"E59.2.1")])]});
            var Q15;
            Q15=makeQuery(id+"F3.opExtrude","SWEPT_EDGE",EDGE,{"disambiguationData":[OSD([sQuery(id+"F1.wireOp",EDGE,"E59.2.1"),sQuery(id+"F1.wireOp",EDGE,"E59.2.2")])]});
            fillet(context, id + "F7", {"entities" : qUnion([Q0, Q1, Q2, Q3, Q4, Q5, Q6, Q7, Q8, Q9, Q10, Q11, Q12, Q13, Q14, Q15]), "radius" : 10 * mm, "tangentPropagation" : true, "allowEdgeOverflow" : false});
        }
        {
            var Q0;
            Q0=qCreatedBy(makeId("Front.planeOp"),FACE);
            var sketch = newSketch(context, id + "F8", { "sketchPlane" : qUnion([Q0])});
            skArc(sketch, "E83", {"start": v(-310, 305) * mm, "mid": v(0, -5) * mm, "end": v(310, 305) * mm});
            skLineSegment(sketch, "E84", {"start": v(0, 305) * mm, "end": v(0, 15) * mm});
            skLineSegment(sketch, "E85", {"start": v(-310, 305) * mm, "end": v(310, 305) * mm});
            skSolve(sketch);
        }
        {
            var Q0;
            Q0=qSketchRegion(id+"F8",true);
            var Q1;
            Q1=sQuery(id+"F8.wireOp",EDGE,"E85");
            revolve(context, id + "F9", {"entities" : qUnion([Q0]), "axis" : qUnion([Q1]), "revolveType" : RevolveType.SYMMETRIC, "angle" : 84.04 * degree});
        }
        {
            var Q0;
            Q0=makeQuery(id+"F9.opRevolve","SWEPT_BODY",BODY,{"disambiguationData":[OSD([sQuery(id+"F8.wireOp",EDGE,"E83"),sQuery(id+"F8.wireOp",EDGE,"E85")])]});
            var Q1;
            Q1=makeQuery(id+"F3.opExtrude","SWEPT_BODY",BODY,{"disambiguationData":[OSD([sQuery(id+"F1.wireOp",EDGE,"E55"),sQuery(id+"F1.wireOp",EDGE,"E56"),sQuery(id+"F1.wireOp",EDGE,"E57"),sQuery(id+"F1.wireOp",EDGE,"E58"),sQuery(id+"F1.wireOp",EDGE,"E59.1.0"),sQuery(id+"F1.wireOp",EDGE,"E59.1.1"),sQuery(id+"F1.wireOp",EDGE,"E59.1.2"),sQuery(id+"F1.wireOp",EDGE,"E59.2.0"),sQuery(id+"F1.wireOp",EDGE,"E59.2.1"),sQuery(id+"F1.wireOp",EDGE,"E59.2.2"),sQuery(id+"F1.wireOp",EDGE,"E59.3.0"),sQuery(id+"F1.wireOp",EDGE,"E59.3.1"),sQuery(id+"F1.wireOp",EDGE,"E59.3.2"),sQuery(id+"F1.wireOp",EDGE,"E59.4.0"),sQuery(id+"F1.wireOp",EDGE,"E59.4.1"),sQuery(id+"F1.wireOp",EDGE,"E59.4.2"),sQuery(id+"F1.wireOp",EDGE,"E59.5.0"),sQuery(id+"F1.wireOp",EDGE,"E59.5.1"),sQuery(id+"F1.wireOp",EDGE,"E59.5.2"),sQuery(id+"F1.wireOp",EDGE,"E59.6.0"),sQuery(id+"F1.wireOp",EDGE,"E59.6.1"),sQuery(id+"F1.wireOp",EDGE,"E59.6.2"),sQuery(id+"F1.wireOp",EDGE,"E59.7.0"),sQuery(id+"F1.wireOp",EDGE,"E59.7.1"),sQuery(id+"F1.wireOp",EDGE,"E59.7.2"),sQuery(id+"F1.wireOp",EDGE,"E60")])]});
            booleanBodies(context, id + "F10", {"operationType" : BooleanOperationType.SUBTRACTION, "tools" : qUnion([Q0]), "targets" : qUnion([Q1])});
        }
        {
            var Q0;
            Q0=qSketchRegion(id+"F2",true);
            extrude(context, id + "F11", {"entities" : qUnion([Q0]), "operationType" : NewBodyOperationType.ADD, "depth" : 20 * mm});
        }
        {
            var Q0;
            Q0=qSketchRegion(id+"F2",true);
            extrude(context, id + "F12", {"entities" : qUnion([Q0]), "operationType" : NewBodyOperationType.ADD, "oppositeDirection" : true, "depth" : 15 * mm});
        }
        {
            var Q0;
            Q0=makeQuery(id+"F3.opExtrude","SWEPT_FACE",FACE,{"disambiguationData":[OSD([sQuery(id+"F1.wireOp",EDGE,"E59.2.1")])]});
            var Q1;
            Q1=makeQuery(id+"F7.opFillet","BLEND_FACE",FACE,{"disambiguationData":[OSD([sQuery(id+"F1.wireOp",EDGE,"E59.2.1"),sQuery(id+"F1.wireOp",EDGE,"E59.2.2")])]});
            var Q2;
            Q2=makeQuery(id+"F3.opExtrude","SWEPT_FACE",FACE,{"disambiguationData":[OSD([sQuery(id+"F1.wireOp",EDGE,"E59.2.2")])]});
            var Q3;
            {var subQ0=sQuery(id+"F1.wireOp",EDGE,"E55");Q3=makeQuery(id+"F3.opExtrude","SWEPT_FACE",FACE,{"disambiguationData":[OSD([subQ0]),TDD([makeQuery(id+"F1.imprint","IMPRINT",EDGE,{"disambiguationData":[TD([[makeQuery(id+"F1.imprint","INTERSECT",VERTEX,{"derivedFrom":[subQ0,sQuery(id+"F1.wireOp",EDGE,"E59.1.0")]}),-1.0]])],"derivedFrom":subQ0})])]});}
            var Q4;
            Q4=makeQuery(id+"F7.opFillet","BLEND_FACE",FACE,{"disambiguationData":[OSD([sQuery(id+"F1.wireOp",EDGE,"E59.2.0"),sQuery(id+"F1.wireOp",EDGE,"E59.2.1")])]});
            var Q5;
            Q5=makeQuery(id+"F3.opExtrude","SWEPT_FACE",FACE,{"disambiguationData":[OSD([sQuery(id+"F1.wireOp",EDGE,"E59.2.0")])]});
            var Q6;
            {var subQ0=sQuery(id+"F1.wireOp",EDGE,"E55");Q6=makeQuery(id+"F3.opExtrude","SWEPT_FACE",FACE,{"disambiguationData":[OSD([subQ0]),TDD([makeQuery(id+"F1.imprint","IMPRINT",EDGE,{"disambiguationData":[TD([[makeQuery(id+"F1.imprint","INTERSECT",VERTEX,{"derivedFrom":[subQ0,sQuery(id+"F1.wireOp",EDGE,"E59.2.0")]}),-1.0]])],"derivedFrom":subQ0})])]});}
            var Q7;
            Q7=makeQuery(id+"F3.opExtrude","SWEPT_FACE",FACE,{"disambiguationData":[OSD([sQuery(id+"F1.wireOp",EDGE,"E59.3.2")])]});
            var Q8;
            Q8=makeQuery(id+"F7.opFillet","BLEND_FACE",FACE,{"disambiguationData":[OSD([sQuery(id+"F1.wireOp",EDGE,"E59.3.1"),sQuery(id+"F1.wireOp",EDGE,"E59.3.2")])]});
            var Q9;
            Q9=makeQuery(id+"F3.opExtrude","SWEPT_FACE",FACE,{"disambiguationData":[OSD([sQuery(id+"F1.wireOp",EDGE,"E59.3.1")])]});
            var Q10;
            Q10=makeQuery(id+"F7.opFillet","BLEND_FACE",FACE,{"disambiguationData":[OSD([sQuery(id+"F1.wireOp",EDGE,"E59.3.0"),sQuery(id+"F1.wireOp",EDGE,"E59.3.1")])]});
            var Q11;
            {var subQ0=sQuery(id+"F1.wireOp",EDGE,"E55");Q11=makeQuery(id+"F3.opExtrude","SWEPT_FACE",FACE,{"disambiguationData":[OSD([subQ0]),TDD([makeQuery(id+"F1.imprint","IMPRINT",EDGE,{"disambiguationData":[TD([[makeQuery(id+"F1.imprint","INTERSECT",VERTEX,{"derivedFrom":[subQ0,sQuery(id+"F1.wireOp",EDGE,"E59.3.0")]}),-1.0]])],"derivedFrom":subQ0})])]});}
            var Q12;
            Q12=makeQuery(id+"F3.opExtrude","SWEPT_FACE",FACE,{"disambiguationData":[OSD([sQuery(id+"F1.wireOp",EDGE,"E59.3.0")])]});
            var Q13;
            Q13=makeQuery(id+"F3.opExtrude","SWEPT_EDGE",EDGE,{"disambiguationData":[OSD([sQuery(id+"F1.wireOp",EDGE,"E55"),sQuery(id+"F1.wireOp",EDGE,"E59.3.0")])]});
            var Q14;
            Q14=makeQuery(id+"F3.opExtrude","SWEPT_FACE",FACE,{"disambiguationData":[OSD([sQuery(id+"F1.wireOp",EDGE,"E59.4.2")])]});
            var Q15;
            Q15=makeQuery(id+"F7.opFillet","BLEND_FACE",FACE,{"disambiguationData":[OSD([sQuery(id+"F1.wireOp",EDGE,"E59.4.1"),sQuery(id+"F1.wireOp",EDGE,"E59.4.2")])]});
            var Q16;
            Q16=makeQuery(id+"F3.opExtrude","SWEPT_FACE",FACE,{"disambiguationData":[OSD([sQuery(id+"F1.wireOp",EDGE,"E59.4.1")])]});
            var Q17;
            Q17=makeQuery(id+"F7.opFillet","BLEND_FACE",FACE,{"disambiguationData":[OSD([sQuery(id+"F1.wireOp",EDGE,"E59.4.0"),sQuery(id+"F1.wireOp",EDGE,"E59.4.1")])]});
            var Q18;
            Q18=makeQuery(id+"F3.opExtrude","SWEPT_FACE",FACE,{"disambiguationData":[OSD([sQuery(id+"F1.wireOp",EDGE,"E59.4.0")])]});
            var Q19;
            {var subQ0=sQuery(id+"F1.wireOp",EDGE,"E55");Q19=makeQuery(id+"F3.opExtrude","SWEPT_FACE",FACE,{"disambiguationData":[OSD([subQ0]),TDD([makeQuery(id+"F1.imprint","IMPRINT",EDGE,{"disambiguationData":[TD([[makeQuery(id+"F1.imprint","INTERSECT",VERTEX,{"derivedFrom":[subQ0,sQuery(id+"F1.wireOp",EDGE,"E59.4.0")]}),-1.0]])],"derivedFrom":subQ0})])]});}
            var Q20;
            Q20=makeQuery(id+"F3.opExtrude","SWEPT_FACE",FACE,{"disambiguationData":[OSD([sQuery(id+"F1.wireOp",EDGE,"E59.5.2")])]});
            var Q21;
            Q21=makeQuery(id+"F7.opFillet","BLEND_FACE",FACE,{"disambiguationData":[OSD([sQuery(id+"F1.wireOp",EDGE,"E59.5.1"),sQuery(id+"F1.wireOp",EDGE,"E59.5.2")])]});
            var Q22;
            Q22=makeQuery(id+"F3.opExtrude","SWEPT_FACE",FACE,{"disambiguationData":[OSD([sQuery(id+"F1.wireOp",EDGE,"E59.5.1")])]});
            var Q23;
            Q23=makeQuery(id+"F7.opFillet","BLEND_FACE",FACE,{"disambiguationData":[OSD([sQuery(id+"F1.wireOp",EDGE,"E59.5.0"),sQuery(id+"F1.wireOp",EDGE,"E59.5.1")])]});
            var Q24;
            Q24=makeQuery(id+"F3.opExtrude","SWEPT_FACE",FACE,{"disambiguationData":[OSD([sQuery(id+"F1.wireOp",EDGE,"E59.5.0")])]});
            var Q25;
            {var subQ0=sQuery(id+"F1.wireOp",EDGE,"E55");Q25=makeQuery(id+"F3.opExtrude","SWEPT_FACE",FACE,{"disambiguationData":[OSD([subQ0]),TDD([makeQuery(id+"F1.imprint","IMPRINT",EDGE,{"disambiguationData":[TD([[makeQuery(id+"F1.imprint","INTERSECT",VERTEX,{"derivedFrom":[subQ0,sQuery(id+"F1.wireOp",EDGE,"E59.5.0")]}),-1.0]])],"derivedFrom":subQ0})])]});}
            var Q26;
            Q26=makeQuery(id+"F3.opExtrude","SWEPT_FACE",FACE,{"disambiguationData":[OSD([sQuery(id+"F1.wireOp",EDGE,"E59.6.2")])]});
            var Q27;
            Q27=makeQuery(id+"F3.opExtrude","SWEPT_FACE",FACE,{"disambiguationData":[OSD([sQuery(id+"F1.wireOp",EDGE,"E59.6.1")])]});
            var Q28;
            Q28=makeQuery(id+"F3.opExtrude","SWEPT_FACE",FACE,{"disambiguationData":[OSD([sQuery(id+"F1.wireOp",EDGE,"E59.6.0")])]});
            var Q29;
            {var subQ0=sQuery(id+"F1.wireOp",EDGE,"E55");Q29=makeQuery(id+"F3.opExtrude","SWEPT_FACE",FACE,{"disambiguationData":[OSD([subQ0]),TDD([makeQuery(id+"F1.imprint","IMPRINT",EDGE,{"disambiguationData":[TD([[makeQuery(id+"F1.imprint","INTERSECT",VERTEX,{"derivedFrom":[subQ0,sQuery(id+"F1.wireOp",EDGE,"E59.6.0")]}),-1.0]])],"derivedFrom":subQ0})])]});}
            var Q30;
            Q30=makeQuery(id+"F3.opExtrude","SWEPT_FACE",FACE,{"disambiguationData":[OSD([sQuery(id+"F1.wireOp",EDGE,"E59.7.1")])]});
            var Q31;
            Q31=makeQuery(id+"F3.opExtrude","SWEPT_FACE",FACE,{"disambiguationData":[OSD([sQuery(id+"F1.wireOp",EDGE,"E59.7.0")])]});
            var Q32;
            {var subQ0=sQuery(id+"F1.wireOp",EDGE,"E55");Q32=makeQuery(id+"F3.opExtrude","SWEPT_FACE",FACE,{"disambiguationData":[OSD([subQ0]),TDD([makeQuery(id+"F1.imprint","IMPRINT",EDGE,{"disambiguationData":[TD([[makeQuery(id+"F1.imprint","INTERSECT",VERTEX,{"derivedFrom":[subQ0,sQuery(id+"F1.wireOp",EDGE,"E58")]}),1.0]])],"derivedFrom":subQ0})])]});}
            var Q33;
            {var subQ0=sQuery(id+"F1.wireOp",EDGE,"E55");Q33=makeQuery(id+"F3.opExtrude","SWEPT_FACE",FACE,{"disambiguationData":[OSD([subQ0]),TDD([makeQuery(id+"F1.imprint","IMPRINT",EDGE,{"disambiguationData":[TD([[makeQuery(id+"F1.imprint","INTERSECT",VERTEX,{"derivedFrom":[subQ0,sQuery(id+"F1.wireOp",EDGE,"E58")]}),1.0]])],"derivedFrom":subQ0})])]});}
            var Q34;
            Q34=makeQuery(id+"F3.opExtrude","SWEPT_FACE",FACE,{"disambiguationData":[OSD([sQuery(id+"F1.wireOp",EDGE,"E58")])]});
            var Q35;
            Q35=makeQuery(id+"F3.opExtrude","SWEPT_FACE",FACE,{"disambiguationData":[OSD([sQuery(id+"F1.wireOp",EDGE,"E57")])]});
            var Q36;
            {var subQ0=sQuery(id+"F1.wireOp",EDGE,"E55");Q36=makeQuery(id+"F3.opExtrude","SWEPT_FACE",FACE,{"disambiguationData":[OSD([subQ0]),TDD([makeQuery(id+"F1.imprint","IMPRINT",EDGE,{"disambiguationData":[TD([[makeQuery(id+"F1.imprint","INTERSECT",VERTEX,{"derivedFrom":[subQ0,sQuery(id+"F1.wireOp",EDGE,"E56")]}),-1.0]])],"derivedFrom":subQ0})])]});}
            var Q37;
            Q37=makeQuery(id+"F3.opExtrude","SWEPT_FACE",FACE,{"disambiguationData":[OSD([sQuery(id+"F1.wireOp",EDGE,"E56")])]});
            var Q38;
            Q38=makeQuery(id+"F3.opExtrude","SWEPT_FACE",FACE,{"disambiguationData":[OSD([sQuery(id+"F1.wireOp",EDGE,"E59.1.2")])]});
            var Q39;
            Q39=makeQuery(id+"F3.opExtrude","SWEPT_FACE",FACE,{"disambiguationData":[OSD([sQuery(id+"F1.wireOp",EDGE,"E59.1.1")])]});
            var Q40;
            Q40=makeQuery(id+"F3.opExtrude","SWEPT_FACE",FACE,{"disambiguationData":[OSD([sQuery(id+"F1.wireOp",EDGE,"E59.1.0")])]});
            fillet(context, id + "F13", {"entities" : qUnion([Q0, Q1, Q2, Q3, Q4, Q5, Q6, Q7, Q8, Q9, Q10, Q11, Q12, Q13, Q14, Q15, Q16, Q17, Q18, Q19, Q20, Q21, Q22, Q23, Q24, Q25, Q26, Q27, Q28, Q29, Q30, Q31, Q32, Q33, Q34, Q35, Q36, Q37, Q38, Q39, Q40]), "radius" : 5 * mm, "tangentPropagation" : true, "allowEdgeOverflow" : false});
        }
        {
            var Q0;
            Q0=makeQuery(id+"F3.opExtrude","CAP_FACE",FACE,{"disambiguationData":[OSD([sQuery(id+"F1.wireOp",EDGE,"E55"),sQuery(id+"F1.wireOp",EDGE,"E56"),sQuery(id+"F1.wireOp",EDGE,"E57"),sQuery(id+"F1.wireOp",EDGE,"E58"),sQuery(id+"F1.wireOp",EDGE,"E59.1.0"),sQuery(id+"F1.wireOp",EDGE,"E59.1.1"),sQuery(id+"F1.wireOp",EDGE,"E59.1.2"),sQuery(id+"F1.wireOp",EDGE,"E59.2.0"),sQuery(id+"F1.wireOp",EDGE,"E59.2.1"),sQuery(id+"F1.wireOp",EDGE,"E59.2.2"),sQuery(id+"F1.wireOp",EDGE,"E59.3.0"),sQuery(id+"F1.wireOp",EDGE,"E59.3.1"),sQuery(id+"F1.wireOp",EDGE,"E59.3.2"),sQuery(id+"F1.wireOp",EDGE,"E59.4.0"),sQuery(id+"F1.wireOp",EDGE,"E59.4.1"),sQuery(id+"F1.wireOp",EDGE,"E59.4.2"),sQuery(id+"F1.wireOp",EDGE,"E59.5.0"),sQuery(id+"F1.wireOp",EDGE,"E59.5.1"),sQuery(id+"F1.wireOp",EDGE,"E59.5.2"),sQuery(id+"F1.wireOp",EDGE,"E59.6.0"),sQuery(id+"F1.wireOp",EDGE,"E59.6.1"),sQuery(id+"F1.wireOp",EDGE,"E59.6.2"),sQuery(id+"F1.wireOp",EDGE,"E59.7.0"),sQuery(id+"F1.wireOp",EDGE,"E59.7.1"),sQuery(id+"F1.wireOp",EDGE,"E59.7.2"),sQuery(id+"F1.wireOp",EDGE,"E60")])],"isStart":false});
            var sketch = newSketch(context, id + "F14", { "sketchPlane" : qUnion([Q0])});
            skCircle(sketch, "E86", {"center": v(0, 128.38) * mm, "radius": 7.5 * mm});
            skPoint(sketch, "E86.centerSnap0", {"position": v(0, 145) * mm});
            skSolve(sketch);
        }
        {
            var Q0;
            Q0=makeQuery(id+"F14.imprint","IMPRINT",FACE,{"disambiguationData":[TD([[makeQuery(id+"F14.imprint","IMPRINT",EDGE,{"derivedFrom":sQuery(id+"F14.wireOp",EDGE,"E86")}),1.0]])]});
            extrude(context, id + "F15", {"entities" : qUnion([Q0]), "operationType" : NewBodyOperationType.REMOVE, "endBound" : BoundingType.THROUGH_ALL, "oppositeDirection" : true, "depth" : 25 * mm});
        }
        {
            var Q0;
            Q0=makeQuery(id+"F15.boolean.opBoolean","COPY",FACE,{"derivedFrom":makeQuery(id+"F15.opExtrude","SWEPT_FACE",FACE,{"disambiguationData":[OSD([sQuery(id+"F14.wireOp",EDGE,"E86")])]})});
            chamfer(context, id + "F16", {"entities" : qUnion([Q0]), "width" : 5 * mm, "tangentPropagation" : true});
        }
    });
